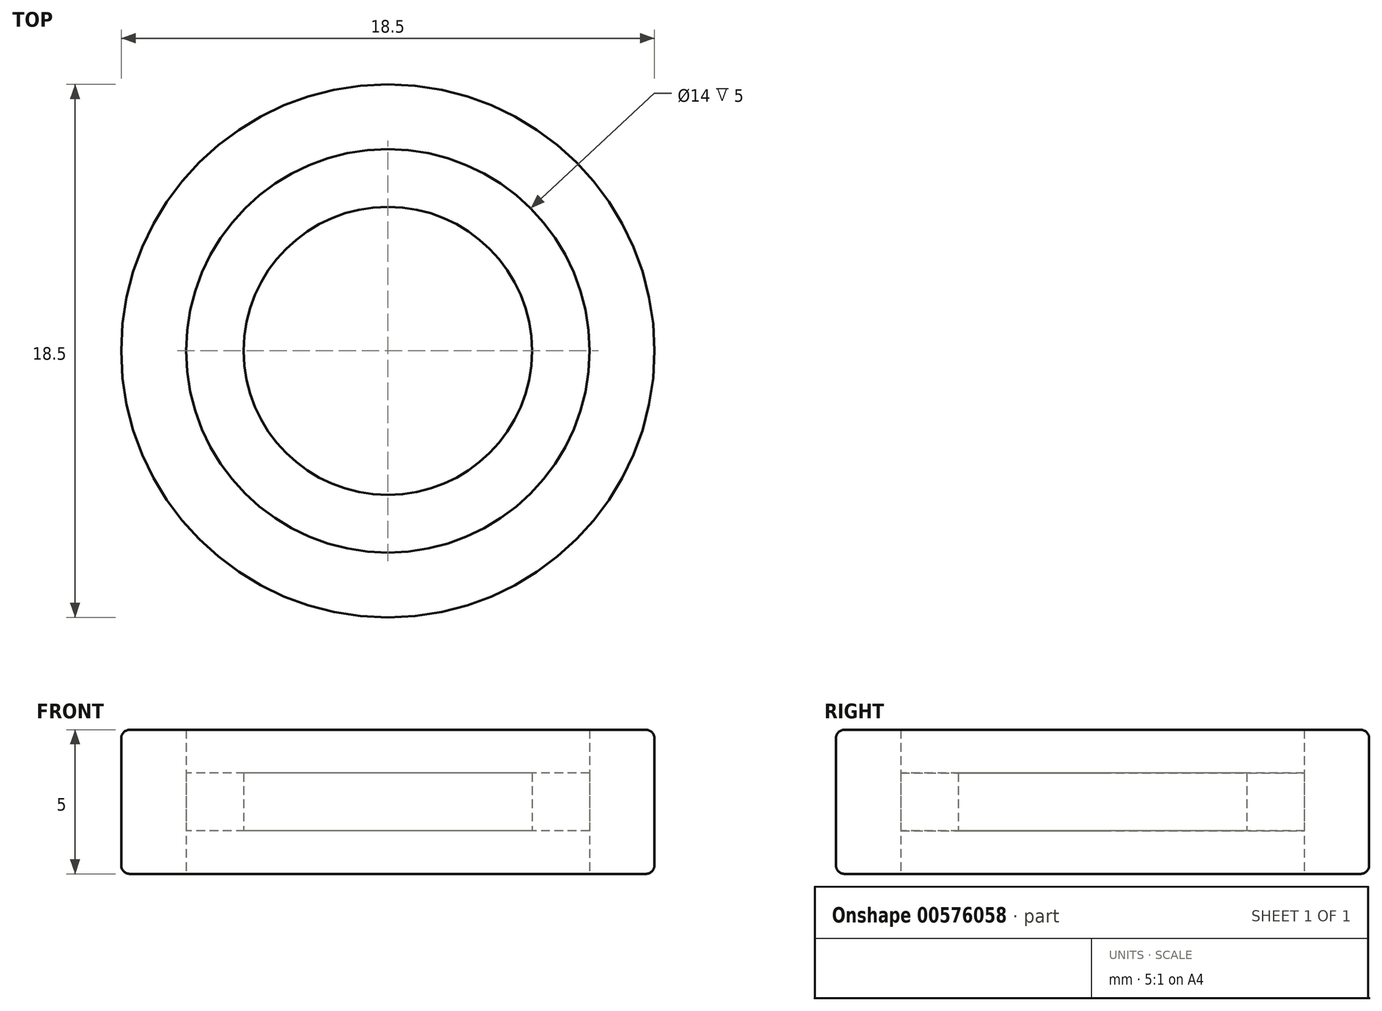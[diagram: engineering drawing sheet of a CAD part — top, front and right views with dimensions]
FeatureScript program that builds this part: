
annotation { "Feature Type Name" : "Feature", "Feature Type Description" : "" }
export const myFeature = defineFeature(function(context is Context, id is Id, definition is map)
    precondition{}
    {
        {
            var Q0;
            Q0=qCreatedBy(makeId("Top.planeOp"),FACE);
            var sketch = newSketch(context, id + "F0", { "sketchPlane" : qUnion([Q0])});
            skCircle(sketch, "E0", {"center": v(0, 0) * mm, "radius": 9.25 * mm});
            skCircle(sketch, "E1", {"center": v(0, 0) * mm, "radius": 7 * mm});
            skCircle(sketch, "E2", {"center": v(0, 0) * mm, "radius": 5 * mm});
            skSolve(sketch);
        }
        {
            var Q0;
            Q0=makeQuery(id+"F0.imprint","IMPRINT",FACE,{"disambiguationData":[TD([[makeQuery(id+"F0.imprint","IMPRINT",EDGE,{"derivedFrom":sQuery(id+"F0.wireOp",EDGE,"E0")}),1.0]])]});
            extrude(context, id + "F1", {"entities" : qUnion([Q0]), "endBound" : BoundingType.SYMMETRIC, "depth" : 5 * mm, "offsetDistance" : 25 * mm});
        }
        {
            var Q0;
            Q0=makeQuery(id+"F0.imprint","IMPRINT",FACE,{"disambiguationData":[TD([[makeQuery(id+"F0.imprint","IMPRINT",EDGE,{"derivedFrom":sQuery(id+"F0.wireOp",EDGE,"E1")}),1.0]])]});
            extrude(context, id + "F2", {"entities" : qUnion([Q0]), "endBound" : BoundingType.SYMMETRIC, "depth" : 2 * mm, "offsetDistance" : 25 * mm});
        }
        {
            var Q0;
            Q0=makeQuery(id+"F1.opExtrude","CAP_EDGE",EDGE,{"disambiguationData":[OSD([sQuery(id+"F0.wireOp",EDGE,"E0")])],"isStart":false});
            var Q1;
            Q1=makeQuery(id+"F1.opExtrude","CAP_EDGE",EDGE,{"disambiguationData":[OSD([sQuery(id+"F0.wireOp",EDGE,"E0")])],"isStart":true});
            fillet(context, id + "F3", {"entities" : qUnion([Q0, Q1]), "radius" : 0.3 * mm, "tangentPropagation" : true, "allowEdgeOverflow" : false});
        }
    });
